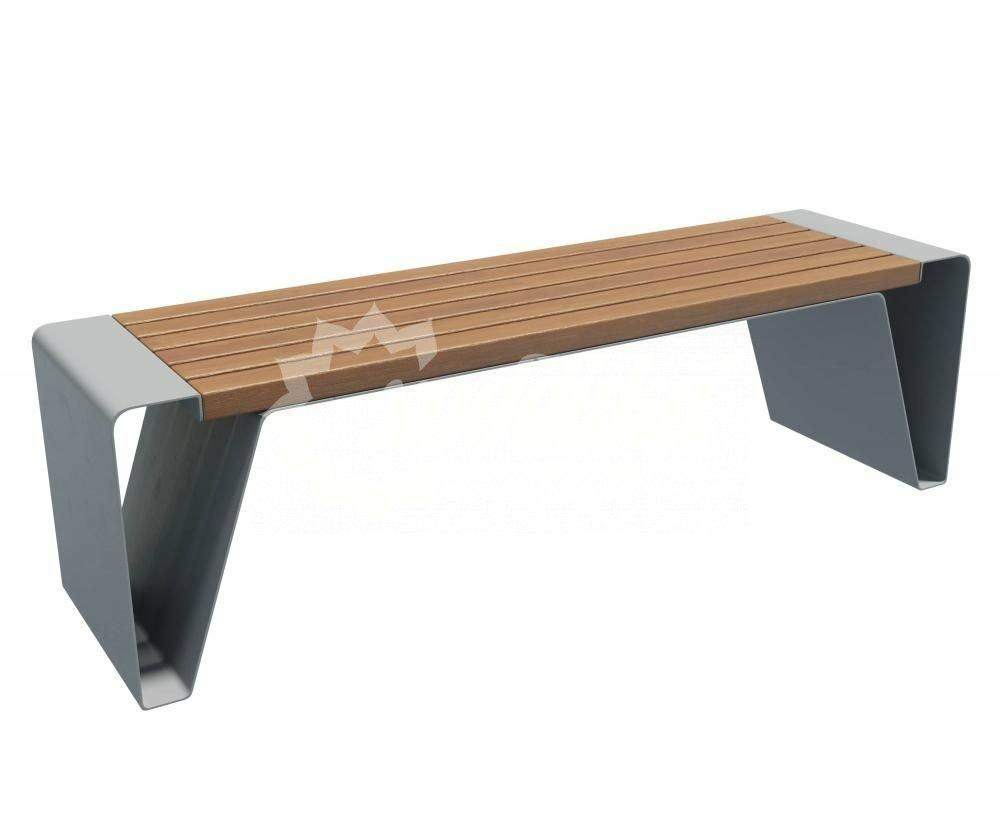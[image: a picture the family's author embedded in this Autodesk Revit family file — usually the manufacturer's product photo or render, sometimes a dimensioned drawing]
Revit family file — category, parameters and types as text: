
# Revit family: 2241 Скамейка стальная «Энигма»  без спинки Хоббика
name_source: partatom
category: Антураж
revit_build: Autodesk Revit 2018 (Build: 20180423_1000(x64)
units: mm (PartAtom-declared; Revit-internal decimal feet)

## family parameters
Всегда вертикально = Да
Источник визуального образа = Геометрия семейства
На основе рабочей плоскости = Нет
Общий = Нет
При загрузке вырезать с полостями = Нет
Точка расчета площади = Нет

## types (2) — shared parameters
URL = hobbyka.ru/product/skameyka_bez_spinki_enigma/
Артикул товара = Арт. 22411
Высота = 445 мм
Группа модели = Скамейки
Изготовитель = ООО «Хоббика»
Изображение типоразмера = Скамейка стальная Энигма без спинки.jpg
Материал изделия = Дерево, сталь
Цвет каркаса = Сталь
Цвет лавки = Орех
Ширина = 410 мм

## per-type parameters (varying)
| type | Версия 2,0 м (2 опоры) | Версия 3,0 м (3 опоры) | Длина | Описание |
| Скамейка стальная «Энигма» без спинки 2,0 м (2 опоры) | Да | Нет | 2000 мм | Скамейка стальная «Энигма» без спинки. Версия 2,0 м (2 опоры) |
| Скамейка стальная «Энигма» без спинки 3,0 м (3 опоры) | Нет | Да | 3000 мм | Скамейка стальная «Энигма» без спинки. Версия 3,0 м (3 опоры) |
